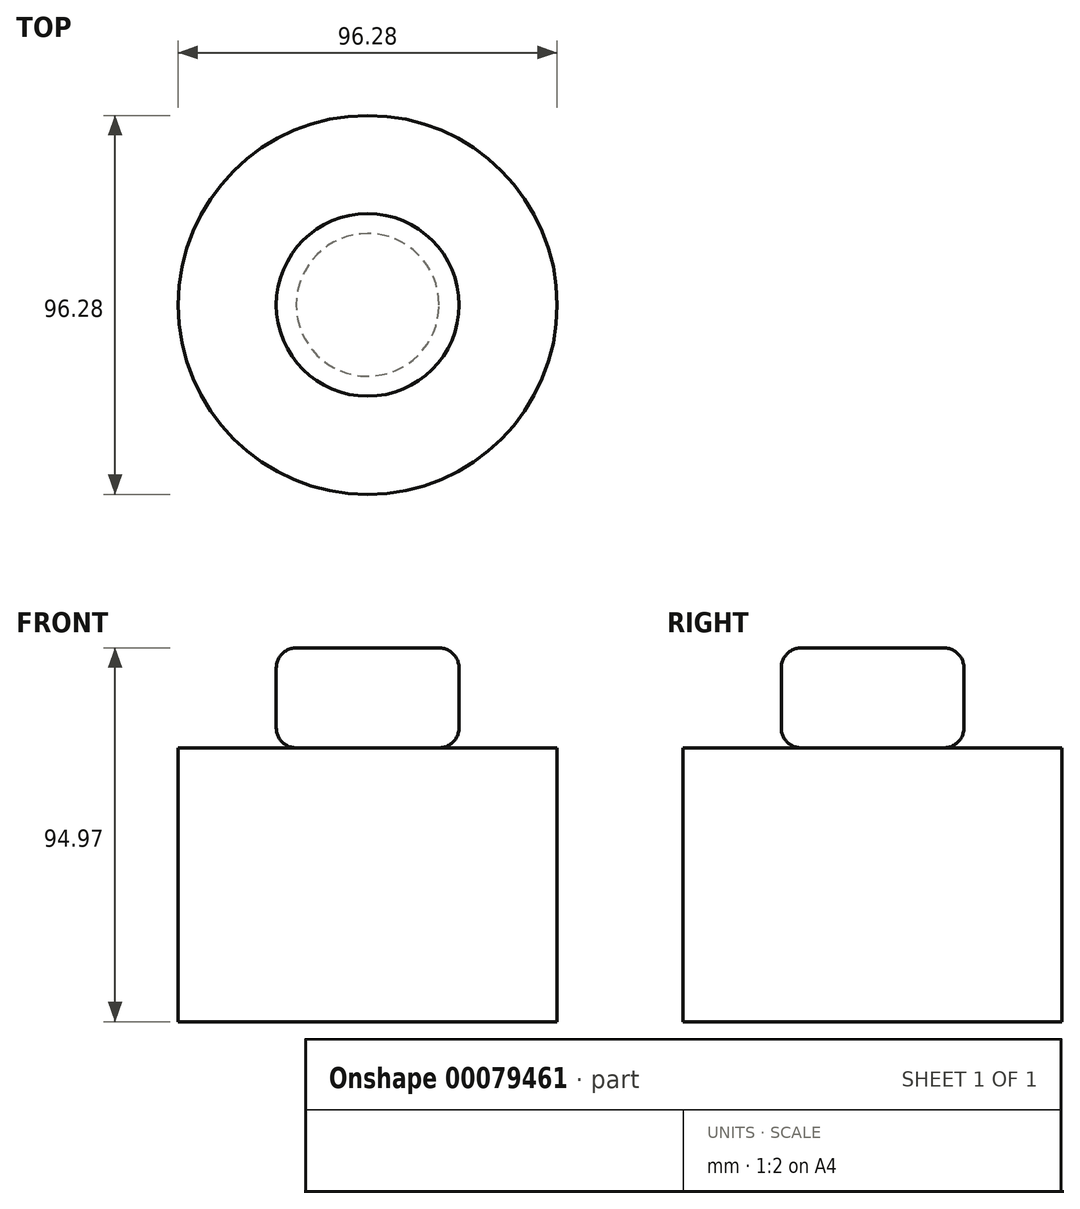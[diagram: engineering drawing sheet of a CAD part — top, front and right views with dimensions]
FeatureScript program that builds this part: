
annotation { "Feature Type Name" : "Feature", "Feature Type Description" : "" }
export const myFeature = defineFeature(function(context is Context, id is Id, definition is map)
    precondition{}
    {
        {
            var Q0;
            Q0=qCreatedBy(makeId("Top.planeOp"),FACE);
            var sketch = newSketch(context, id + "F0", { "sketchPlane" : qUnion([Q0])});
            skCircle(sketch, "E0", {"center": v(0, 0) * mm, "radius": 23.2 * mm});
            skSolve(sketch);
        }
        {
            var Q0;
            Q0 = qSketchRegion(id + "F0", true);
            extrude(context, id + "F1", {"entities" : qUnion([Q0]), "depth" : 25.4 * mm});
        }
        {
            var Q0;
            Q0=makeQuery(id+"F1.opExtrude","CAP_EDGE",EDGE,{"disambiguationData":[OSD([sQuery(id+"F0.wireOp",EDGE,"E0")])],"isStart":true});
            var Q1;
            Q1=makeQuery(id+"F1.opExtrude","CAP_EDGE",EDGE,{"disambiguationData":[OSD([sQuery(id+"F0.wireOp",EDGE,"E0")])],"isStart":false});
            fillet(context, id + "F2", {"entities" : qUnion([Q0, Q1]), "radius" : 5.08 * mm, "tangentPropagation" : true, "allowEdgeOverflow" : false});
        }
        {
            var Q0;
            Q0=makeQuery(id+"F1.opExtrude","CAP_FACE",FACE,{"disambiguationData":[OSD([sQuery(id+"F0.wireOp",EDGE,"E0")])],"isStart":true});
            var sketch = newSketch(context, id + "F3", { "sketchPlane" : qUnion([Q0])});
            skCircle(sketch, "E1", {"center": v(0, 0) * mm, "radius": 48.14 * mm});
            skSolve(sketch);
        }
        {
            var Q0;
            Q0 = qSketchRegion(id + "F3", true);
            extrude(context, id + "F4", {"entities" : qUnion([Q0]), "operationType" : NewBodyOperationType.ADD, "depth" : 69.57 * mm});
        }
    });
